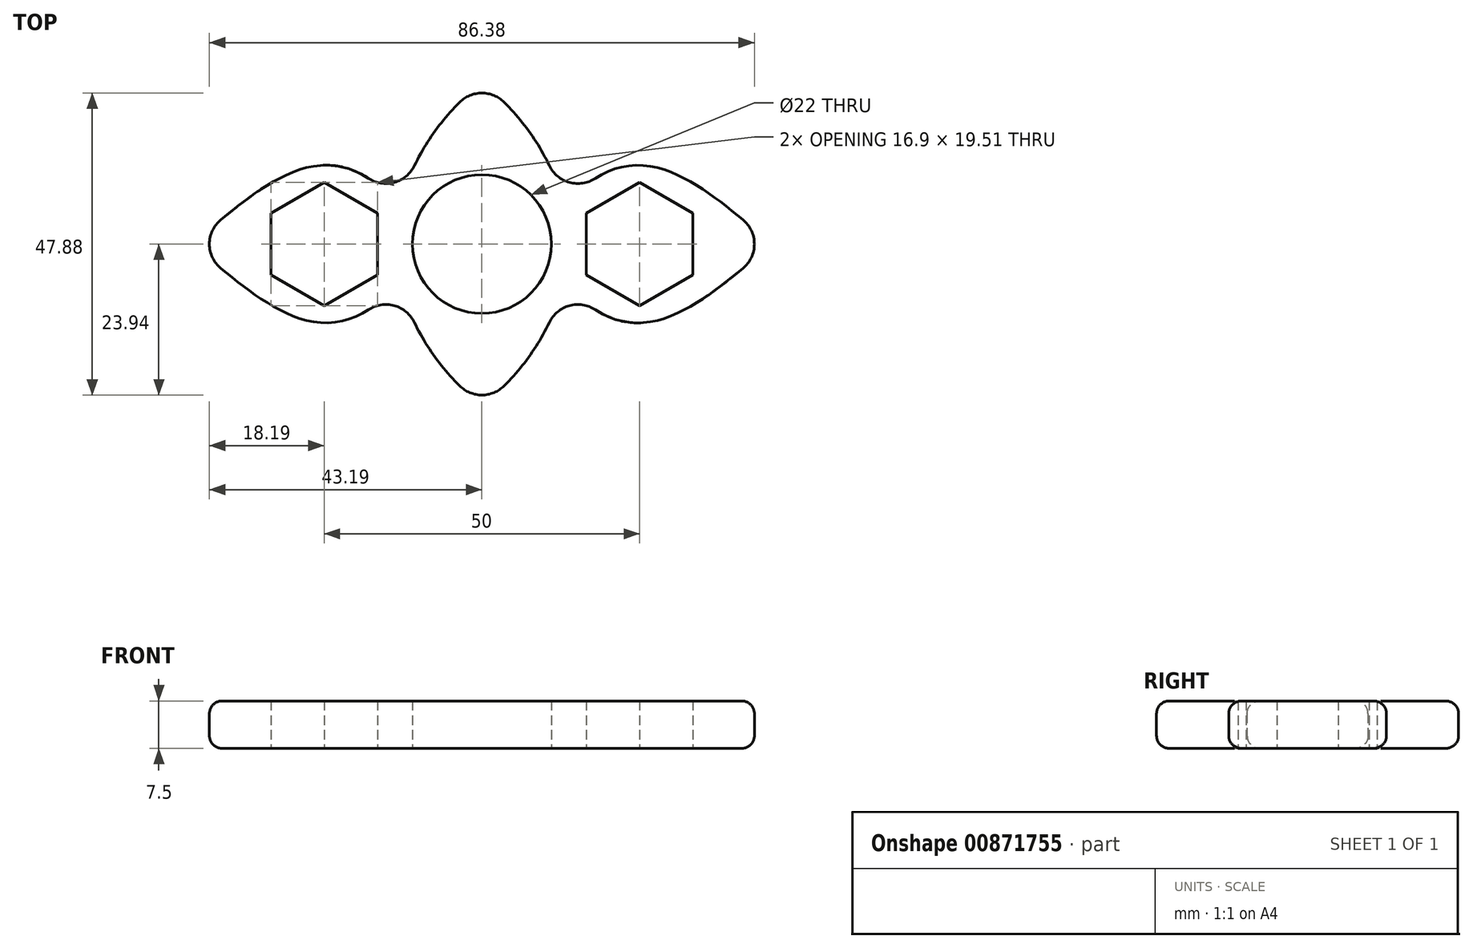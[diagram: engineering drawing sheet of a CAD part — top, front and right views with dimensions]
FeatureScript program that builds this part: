
annotation { "Feature Type Name" : "Feature", "Feature Type Description" : "" }
export const myFeature = defineFeature(function(context is Context, id is Id, definition is map)
    precondition{}
    {
        {
            var Q0;
            Q0=qCreatedBy(makeId("Top.planeOp"),FACE);
            var sketch = newSketch(context, id + "F0", { "sketchPlane" : qUnion([Q0])});
            skCircle(sketch, "E0", {"center": v(0, 0) * mm, "radius": 11 * mm});
            skCircle(sketch, "E1.cCircle", {"center": v(-25, 0) * mm, "radius": 8.45 * mm, "construction": true});
            skLineSegment(sketch, "E1.0", {"start": v(-16.55, 4.88) * mm, "end": v(-16.55, -4.88) * mm});
            skLineSegment(sketch, "E1.1", {"start": v(-16.55, -4.88) * mm, "end": v(-25, -9.76) * mm});
            skLineSegment(sketch, "E1.2", {"start": v(-25, -9.76) * mm, "end": v(-33.45, -4.88) * mm});
            skLineSegment(sketch, "E1.3", {"start": v(-33.45, -4.88) * mm, "end": v(-33.45, 4.88) * mm});
            skLineSegment(sketch, "E1.4", {"start": v(-33.45, 4.88) * mm, "end": v(-25, 9.76) * mm});
            skLineSegment(sketch, "E1.5", {"start": v(-25, 9.76) * mm, "end": v(-16.55, 4.88) * mm});
            skPoint(sketch, "E1.0.midPoint", {"position": v(-16.55, 0) * mm});
            skLineSegment(sketch, "E2.MirrorCS", {"start": v(25, 9.76) * mm, "end": v(16.55, 4.88) * mm});
            skLineSegment(sketch, "E3.MirrorCS", {"start": v(33.45, 4.88) * mm, "end": v(25, 9.76) * mm});
            skLineSegment(sketch, "E4.MirrorCS", {"start": v(33.45, -4.88) * mm, "end": v(33.45, 4.88) * mm});
            skLineSegment(sketch, "E5.MirrorCS", {"start": v(25, -9.76) * mm, "end": v(33.45, -4.88) * mm});
            skLineSegment(sketch, "E6.MirrorCS", {"start": v(16.55, -4.88) * mm, "end": v(25, -9.76) * mm});
            skLineSegment(sketch, "E7.MirrorCS", {"start": v(16.55, 4.88) * mm, "end": v(16.55, -4.88) * mm});
            skArc(sketch, "E8", {"start": v(-13.3, 4.39) * mm, "mid": v(-37.5, 0) * mm, "end": v(-13.3, -4.39) * mm, "construction": true});
            skFitSpline(sketch, "E9", {"points": [v(-13.3, 4.39) * mm, v(-25, 12.5) * mm, v(-45.96, 0) * mm], "startDerivative": vector(-11.1, 34.08) * mm, "endDerivative": vector(-39.79, -33.6) * mm});
            skArc(sketch, "E10.MirrorCS", {"start": v(-13.3, -4.39) * mm, "mid": v(-37.5, 0) * mm, "end": v(-13.3, 4.39) * mm, "construction": true});
            skFitSpline(sketch, "E11.MirrorCS", {"points": [v(-13.3, -4.39) * mm, v(-25, -12.5) * mm, v(-45.96, 0) * mm], "startDerivative": vector(-11.1, -34.08) * mm, "endDerivative": vector(-39.79, 33.6) * mm});
            skFitSpline(sketch, "E12.MirrorCS", {"points": [v(13.3, 4.39) * mm, v(25, 12.5) * mm, v(45.96, 0) * mm], "startDerivative": vector(11.1, 34.08) * mm, "endDerivative": vector(39.79, -33.6) * mm});
            skFitSpline(sketch, "E13.MirrorCS", {"points": [v(13.3, -4.39) * mm, v(25, -12.5) * mm, v(45.96, 0) * mm], "startDerivative": vector(11.1, -34.08) * mm, "endDerivative": vector(39.79, 33.6) * mm});
            skFitSpline(sketch, "E14", {"points": [v(-13.3, 4.39) * mm, v(-8.97, 15.6) * mm, v(0, 25.62) * mm], "startDerivative": vector(4.39, 25.14) * mm, "endDerivative": vector(22.01, 17.4) * mm});
            skFitSpline(sketch, "E15.MirrorCS", {"points": [v(13.3, 4.39) * mm, v(8.97, 15.6) * mm, v(0, 25.62) * mm], "startDerivative": vector(-4.39, 25.14) * mm, "endDerivative": vector(-22.01, 17.4) * mm});
            skFitSpline(sketch, "E16.MirrorCS", {"points": [v(13.3, -4.39) * mm, v(8.97, -15.6) * mm, v(0, -25.62) * mm], "startDerivative": vector(-4.39, -25.14) * mm, "endDerivative": vector(-22.01, -17.4) * mm});
            skFitSpline(sketch, "E17.MirrorCS", {"points": [v(-13.3, -4.39) * mm, v(-8.97, -15.6) * mm, v(0, -25.62) * mm], "startDerivative": vector(4.39, -25.14) * mm, "endDerivative": vector(22.01, -17.4) * mm});
            skSolve(sketch);
        }
        {
            var Q0;
            Q0=makeQuery(id+"F0.imprint","IMPRINT",FACE,{"disambiguationData":[TD([[makeQuery(id+"F0.imprint","IMPRINT",EDGE,{"derivedFrom":sQuery(id+"F0.wireOp",EDGE,"XWGYyqkz-SXJP-u87v-nmEi-YTEFEBtCNdNO")}),1.0]])]});
            var Q1;
            Q1=makeQuery(id+"F0.imprint","IMPRINT",FACE,{"disambiguationData":[TD([[makeQuery(id+"F0.imprint","IMPRINT",EDGE,{"derivedFrom":sQuery(id+"F0.wireOp",EDGE,"E0")}),-1.0]])]});
            extrude(context, id + "F1", {"entities" : qUnion([Q0, Q1]), "depth" : 7.5 * mm, "offsetDistance" : 25 * mm});
        }
        {
            var Q0;
            Q0=makeQuery(id+"F1.opExtrude","SWEPT_EDGE",EDGE,{"disambiguationData":[OSD([sQuery(id+"F0.wireOp",EDGE,"E11.MirrorCS"),sQuery(id+"F0.wireOp",EDGE,"E17.MirrorCS")])]});
            var Q1;
            Q1=makeQuery(id+"F1.opExtrude","SWEPT_EDGE",EDGE,{"disambiguationData":[OSD([sQuery(id+"F0.wireOp",EDGE,"E13.MirrorCS"),sQuery(id+"F0.wireOp",EDGE,"E16.MirrorCS")])]});
            var Q2;
            Q2=makeQuery(id+"F1.opExtrude","SWEPT_EDGE",EDGE,{"disambiguationData":[OSD([sQuery(id+"F0.wireOp",EDGE,"E12.MirrorCS"),sQuery(id+"F0.wireOp",EDGE,"E15.MirrorCS")])]});
            var Q3;
            Q3=makeQuery(id+"F1.opExtrude","SWEPT_EDGE",EDGE,{"disambiguationData":[OSD([sQuery(id+"F0.wireOp",EDGE,"E9"),sQuery(id+"F0.wireOp",EDGE,"E14")])]});
            fillet(context, id + "F2", {"entities" : qUnion([Q0, Q1, Q2, Q3]), "radius" : 5 * mm, "tangentPropagation" : true, "allowEdgeOverflow" : false});
        }
        {
            var Q0;
            Q0=makeQuery(id+"F1.opExtrude","SWEPT_EDGE",EDGE,{"disambiguationData":[OSD([sQuery(id+"F0.wireOp",EDGE,"E12.MirrorCS"),sQuery(id+"F0.wireOp",EDGE,"E13.MirrorCS")])]});
            var Q1;
            Q1=makeQuery(id+"F1.opExtrude","SWEPT_EDGE",EDGE,{"disambiguationData":[OSD([sQuery(id+"F0.wireOp",EDGE,"E9"),sQuery(id+"F0.wireOp",EDGE,"E11.MirrorCS")])]});
            var Q2;
            Q2=makeQuery(id+"F1.opExtrude","SWEPT_EDGE",EDGE,{"disambiguationData":[OSD([sQuery(id+"F0.wireOp",EDGE,"E14"),sQuery(id+"F0.wireOp",EDGE,"E15.MirrorCS")])]});
            var Q3;
            Q3=makeQuery(id+"F1.opExtrude","SWEPT_EDGE",EDGE,{"disambiguationData":[OSD([sQuery(id+"F0.wireOp",EDGE,"E16.MirrorCS"),sQuery(id+"F0.wireOp",EDGE,"E17.MirrorCS")])]});
            fillet(context, id + "F3", {"entities" : qUnion([Q0, Q1, Q2, Q3]), "radius" : 5 * mm, "tangentPropagation" : true, "allowEdgeOverflow" : false});
        }
        {
            var Q0;
            Q0=makeQuery(id+"F1.opExtrude","CAP_EDGE",EDGE,{"disambiguationData":[OSD([sQuery(id+"F0.wireOp",EDGE,"XWGYyqkz-SXJP-u87v-nmEi-YTEFEBtCNdNO")])],"isStart":false});
            var Q1;
            {var subQ0=sQuery(id+"F0.wireOp",EDGE,"E11.MirrorCS");var subQ1=sQuery(id+"F0.wireOp",EDGE,"XWGYyqkz-SXJP-u87v-nmEi-YTEFEBtCNdNO");Q1=makeQuery(id+"F2.opFillet","BLEND_EDGE",EDGE,{"blendedFrom":[makeQuery(id+"F1.opExtrude","SWEPT_EDGE",EDGE,{"disambiguationData":[OSD([subQ1,subQ0])]}),makeQuery(id+"F1.opExtrude","CAP_FACE",FACE,{"disambiguationData":[OSD([subQ1,sQuery(id+"F0.wireOp",EDGE,"E0"),sQuery(id+"F0.wireOp",EDGE,"E1.0"),sQuery(id+"F0.wireOp",EDGE,"E1.1"),sQuery(id+"F0.wireOp",EDGE,"E1.2"),sQuery(id+"F0.wireOp",EDGE,"E1.3"),sQuery(id+"F0.wireOp",EDGE,"E1.4"),sQuery(id+"F0.wireOp",EDGE,"E1.5"),sQuery(id+"F0.wireOp",EDGE,"E2.MirrorCS"),sQuery(id+"F0.wireOp",EDGE,"E3.MirrorCS"),sQuery(id+"F0.wireOp",EDGE,"E4.MirrorCS"),sQuery(id+"F0.wireOp",EDGE,"E5.MirrorCS"),sQuery(id+"F0.wireOp",EDGE,"E6.MirrorCS"),sQuery(id+"F0.wireOp",EDGE,"E7.MirrorCS"),sQuery(id+"F0.wireOp",EDGE,"7da6ca97-5263-45d6-8e5d-04a1baefaf0e.trimOffspring"),sQuery(id+"F0.wireOp",EDGE,"E9"),subQ0,sQuery(id+"F0.wireOp",EDGE,"E12.MirrorCS"),sQuery(id+"F0.wireOp",EDGE,"E13.MirrorCS")])],"isStart":true})],"blendedInto":[makeQuery(id+"F1.opExtrude","CAP_FACE",FACE,{"disambiguationData":[OSD([subQ1,sQuery(id+"F0.wireOp",EDGE,"E0"),sQuery(id+"F0.wireOp",EDGE,"E1.0"),sQuery(id+"F0.wireOp",EDGE,"E1.1"),sQuery(id+"F0.wireOp",EDGE,"E1.2"),sQuery(id+"F0.wireOp",EDGE,"E1.3"),sQuery(id+"F0.wireOp",EDGE,"E1.4"),sQuery(id+"F0.wireOp",EDGE,"E1.5"),sQuery(id+"F0.wireOp",EDGE,"E2.MirrorCS"),sQuery(id+"F0.wireOp",EDGE,"E3.MirrorCS"),sQuery(id+"F0.wireOp",EDGE,"E4.MirrorCS"),sQuery(id+"F0.wireOp",EDGE,"E5.MirrorCS"),sQuery(id+"F0.wireOp",EDGE,"E6.MirrorCS"),sQuery(id+"F0.wireOp",EDGE,"E7.MirrorCS"),sQuery(id+"F0.wireOp",EDGE,"7da6ca97-5263-45d6-8e5d-04a1baefaf0e.trimOffspring"),sQuery(id+"F0.wireOp",EDGE,"E9"),subQ0,sQuery(id+"F0.wireOp",EDGE,"E12.MirrorCS"),sQuery(id+"F0.wireOp",EDGE,"E13.MirrorCS")])],"isStart":true})]});}
            var Q2;
            Q2=makeQuery(id+"F1.opExtrude","CAP_EDGE",EDGE,{"disambiguationData":[OSD([sQuery(id+"F0.wireOp",EDGE,"E14")])],"isStart":false});
            fillet(context, id + "F4", {"entities" : qUnion([Q0, Q1, Q2]), "radius" : 2 * mm, "tangentPropagation" : true, "allowEdgeOverflow" : false});
        }
    });
